AUTODESK INVENTOR PART (.ipt)
format: ipt  version: 2022 (Build 260153000, 153)  size: 330,240 bytes
history: native  units: mm
features: extrude x4, sketch x3, projected_geometry x2, shell x1, thicken_offset x1
ambient origin geometry x8: Origin, YZ Plane, XZ Plane, XY Plane, X Axis, Y Axis, Z Axis, Center Point
bodies: Solid1 (feature_tree)
feature tree (11):
  extrude  "Extrusion1"  Depth=3.0mm
  shell  "Shell1"  Thickness=1.0mm
  thicken_offset  "Thicken1"
  extrude  "Extrusion24"  Depth=100.0mm TaperAngle=0.0deg
  sketch  "Sketch47"  dims[d223=2.0mm d224=8.0mm d225=10.0mm d226=2.0mm d227=300.0mm d228=302.0mm d230=280.0mm d231=282.0mm d232=100.0mm d233=0.0mm d234=4.0mm d235=0.0mm]
  extrude  "Extrusion25"  Depth=280.0mm
  extrude  "Extrusion26"  Depth=10.0mm
  sketch  "Sketch3"  dims[d0=4.0mm d1=0.0mm d2=3.0mm d159=1.0mm d160=2.0mm]
  sketch  "Sketch46"  dims[d220=200.0mm d221=100.0mm d222=0.0mm]
  projected_geometry  "Projected Loop27"
  projected_geometry  "Projected Loop28"
